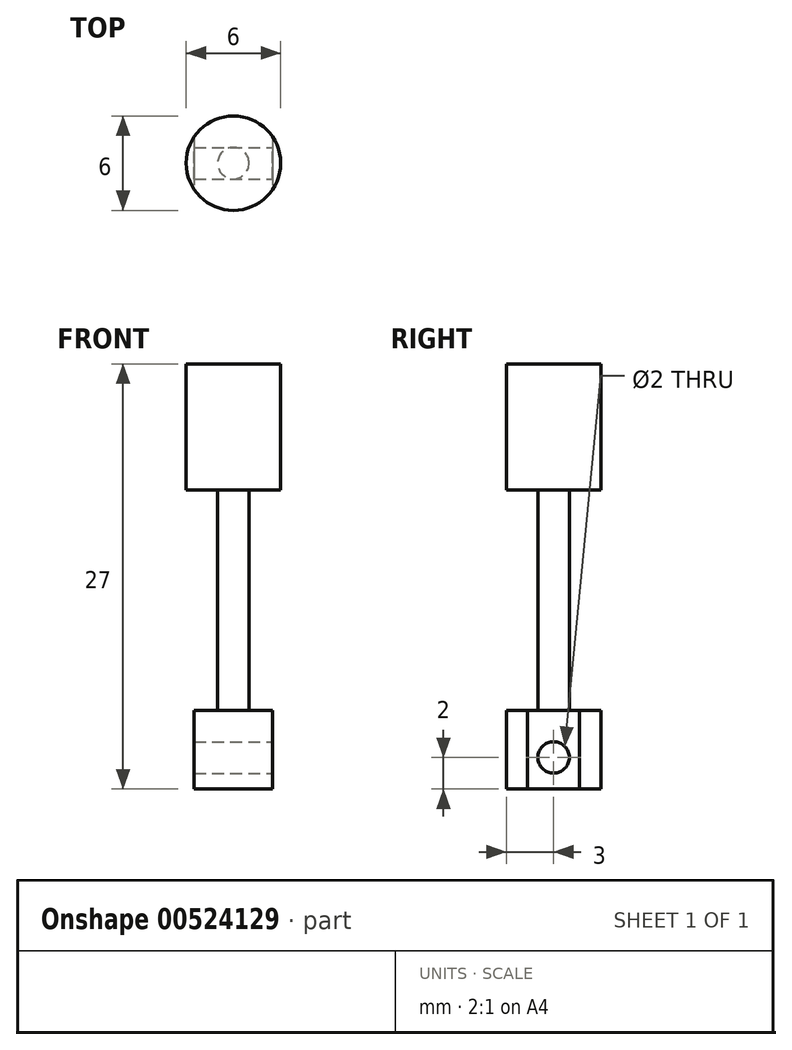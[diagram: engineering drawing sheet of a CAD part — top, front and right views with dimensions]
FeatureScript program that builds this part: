
annotation { "Feature Type Name" : "Feature", "Feature Type Description" : "" }
export const myFeature = defineFeature(function(context is Context, id is Id, definition is map)
    precondition{}
    {
        {
            var Q0;
            Q0=qCreatedBy(makeId("Right.planeOp"),FACE);
            var sketch = newSketch(context, id + "F0", { "sketchPlane" : qUnion([Q0])});
            skLineSegment(sketch, "E0", {"start": v(0, 0) * mm, "end": v(3, 0) * mm});
            skLineSegment(sketch, "E1", {"start": v(3, 0) * mm, "end": v(3, 5) * mm});
            skLineSegment(sketch, "E2", {"start": v(3, 5) * mm, "end": v(1, 5) * mm});
            skLineSegment(sketch, "E3", {"start": v(1, 5) * mm, "end": v(1, 19) * mm});
            skLineSegment(sketch, "E4", {"start": v(1, 19) * mm, "end": v(3, 19) * mm});
            skLineSegment(sketch, "E5", {"start": v(3, 19) * mm, "end": v(3, 27) * mm});
            skLineSegment(sketch, "E6", {"start": v(3, 27) * mm, "end": v(0, 27) * mm});
            skLineSegment(sketch, "E7", {"start": v(0, 27) * mm, "end": v(0, 0) * mm});
            skLineSegment(sketch, "E8", {"start": v(0, 0) * mm, "end": v(0, 29.4) * mm, "construction": true});
            skSolve(sketch);
        }
        {
            var Q0;
            Q0=makeQuery(id+"F0.imprint","IMPRINT",FACE,{"disambiguationData":[TD([[makeQuery(id+"F0.imprint","IMPRINT",EDGE,{"derivedFrom":sQuery(id+"F0.wireOp",EDGE,"E0")}),1.0]])]});
            var Q1;
            Q1=sQuery(id+"F0.wireOp",EDGE,"E8");
            revolve(context, id + "F1", {"entities" : qUnion([Q0]), "axis" : qUnion([Q1]), "revolveType" : RevolveType.FULL});
        }
        {
            var Q0;
            Q0=makeQuery(id+"F1.opRevolve","SWEPT_FACE",FACE,{"disambiguationData":[OSD([sQuery(id+"F0.wireOp",EDGE,"E0")])]});
            var sketch = newSketch(context, id + "F2", { "sketchPlane" : qUnion([Q0])});
            skLineSegment(sketch, "E9.bottom", {"start": v(3.13, -2.99) * mm, "end": v(2.5, -2.99) * mm});
            skLineSegment(sketch, "E9.top", {"start": v(3.13, 3.06) * mm, "end": v(2.5, 3.06) * mm});
            skLineSegment(sketch, "E9.left", {"start": v(3.13, -2.99) * mm, "end": v(3.13, 3.06) * mm});
            skLineSegment(sketch, "E9.right", {"start": v(2.5, -2.99) * mm, "end": v(2.5, 3.06) * mm});
            skSolve(sketch);
        }
        {
            var Q0;
            {var subQ1=sQuery(id+"F2.wireOp",EDGE,"E9.bottom");Q0=makeQuery(id+"F2.imprint","IMPRINT",FACE,{"disambiguationData":[TD([[makeQuery(id+"F2.imprint","IMPRINT",EDGE,{"derivedFrom":subQ1}),-1.0]])]});}
            var Q1;
            {var subQ0=sQuery(id+"F2.wireOp",EDGE,"E9.right");var subQ1=makeQuery(id+"F1.opRevolve","SWEPT_EDGE",EDGE,{"disambiguationData":[OSD([sQuery(id+"F0.wireOp",EDGE,"E0"),sQuery(id+"F0.wireOp",EDGE,"E1")])]});var subQ2=makeQuery(id+"F2.imprint","INTERSECT",VERTEX,{"disambiguationData":[OD(0.0)],"derivedFrom":[subQ1,subQ0]});Q1=makeQuery(id+"F2.imprint","IMPRINT",FACE,{"disambiguationData":[TD([[makeQuery(id+"F2.imprint","IMPRINT",EDGE,{"disambiguationData":[TD([[subQ2,-1.0]])],"derivedFrom":subQ0}),-1.0]])]});}
            extrude(context, id + "F3", {"entities" : qUnion([Q0, Q1]), "operationType" : NewBodyOperationType.REMOVE, "oppositeDirection" : true, "depth" : 6 * mm, "offsetDistance" : 25 * mm});
        }
        {
            var Q0;
            Q0=makeQuery(id+"F1.opRevolve","SWEPT_FACE",FACE,{"disambiguationData":[OSD([sQuery(id+"F0.wireOp",EDGE,"E0")])]});
            var sketch = newSketch(context, id + "F4", { "sketchPlane" : qUnion([Q0])});
            skLineSegment(sketch, "E10.bottom", {"start": v(-2.5, -4.03) * mm, "end": v(-5.04, -4.03) * mm});
            skLineSegment(sketch, "E10.top", {"start": v(-2.5, 4.43) * mm, "end": v(-5.04, 4.43) * mm});
            skLineSegment(sketch, "E10.left", {"start": v(-2.5, -4.03) * mm, "end": v(-2.5, 4.43) * mm});
            skLineSegment(sketch, "E10.right", {"start": v(-5.04, -4.03) * mm, "end": v(-5.04, 4.43) * mm});
            skSolve(sketch);
        }
        {
            var Q0;
            {var subQ4=sQuery(id+"F4.wireOp",EDGE,"E10.bottom");Q0=makeQuery(id+"F4.imprint","IMPRINT",FACE,{"disambiguationData":[TD([[makeQuery(id+"F4.imprint","IMPRINT",EDGE,{"derivedFrom":subQ4}),-1.0]])]});}
            var Q1;
            {var subQ0=sQuery(id+"F4.wireOp",EDGE,"E10.left");var subQ1=makeQuery(id+"F1.opRevolve","SWEPT_EDGE",EDGE,{"disambiguationData":[OSD([sQuery(id+"F0.wireOp",EDGE,"E0"),sQuery(id+"F0.wireOp",EDGE,"E1")])]});var subQ2=makeQuery(id+"F4.imprint","INTERSECT",VERTEX,{"disambiguationData":[OD(0.0)],"derivedFrom":[subQ1,subQ0]});Q1=makeQuery(id+"F4.imprint","IMPRINT",FACE,{"disambiguationData":[TD([[makeQuery(id+"F4.imprint","IMPRINT",EDGE,{"disambiguationData":[TD([[subQ2,-1.0]])],"derivedFrom":subQ0}),1.0]])]});}
            extrude(context, id + "F5", {"entities" : qUnion([Q0, Q1]), "operationType" : NewBodyOperationType.REMOVE, "oppositeDirection" : true, "depth" : 6 * mm, "offsetDistance" : 25 * mm});
        }
        {
            var Q0;
            Q0=makeQuery(id+"F3.boolean.opBoolean","COPY",FACE,{"derivedFrom":makeQuery(id+"F3.opExtrude","SWEPT_FACE",FACE,{"disambiguationData":[OSD([sQuery(id+"F2.wireOp",EDGE,"E9.right")])]})});
            var sketch = newSketch(context, id + "F6", { "sketchPlane" : qUnion([Q0])});
            skCircle(sketch, "E11", {"center": v(0, 2) * mm, "radius": 1 * mm});
            skPoint(sketch, "E11.centerSnap0", {"position": v(-1.66, 2.5) * mm});
            skSolve(sketch);
        }
        {
            var Q0;
            Q0=makeQuery(id+"F6.imprint","IMPRINT",FACE,{"disambiguationData":[TD([[makeQuery(id+"F6.imprint","IMPRINT",EDGE,{"derivedFrom":sQuery(id+"F6.wireOp",EDGE,"E11")}),1.0]])]});
            extrude(context, id + "F7", {"entities" : qUnion([Q0]), "operationType" : NewBodyOperationType.REMOVE, "endBound" : BoundingType.THROUGH_ALL, "oppositeDirection" : true, "depth" : 25 * mm, "offsetDistance" : 25 * mm});
        }
    });
